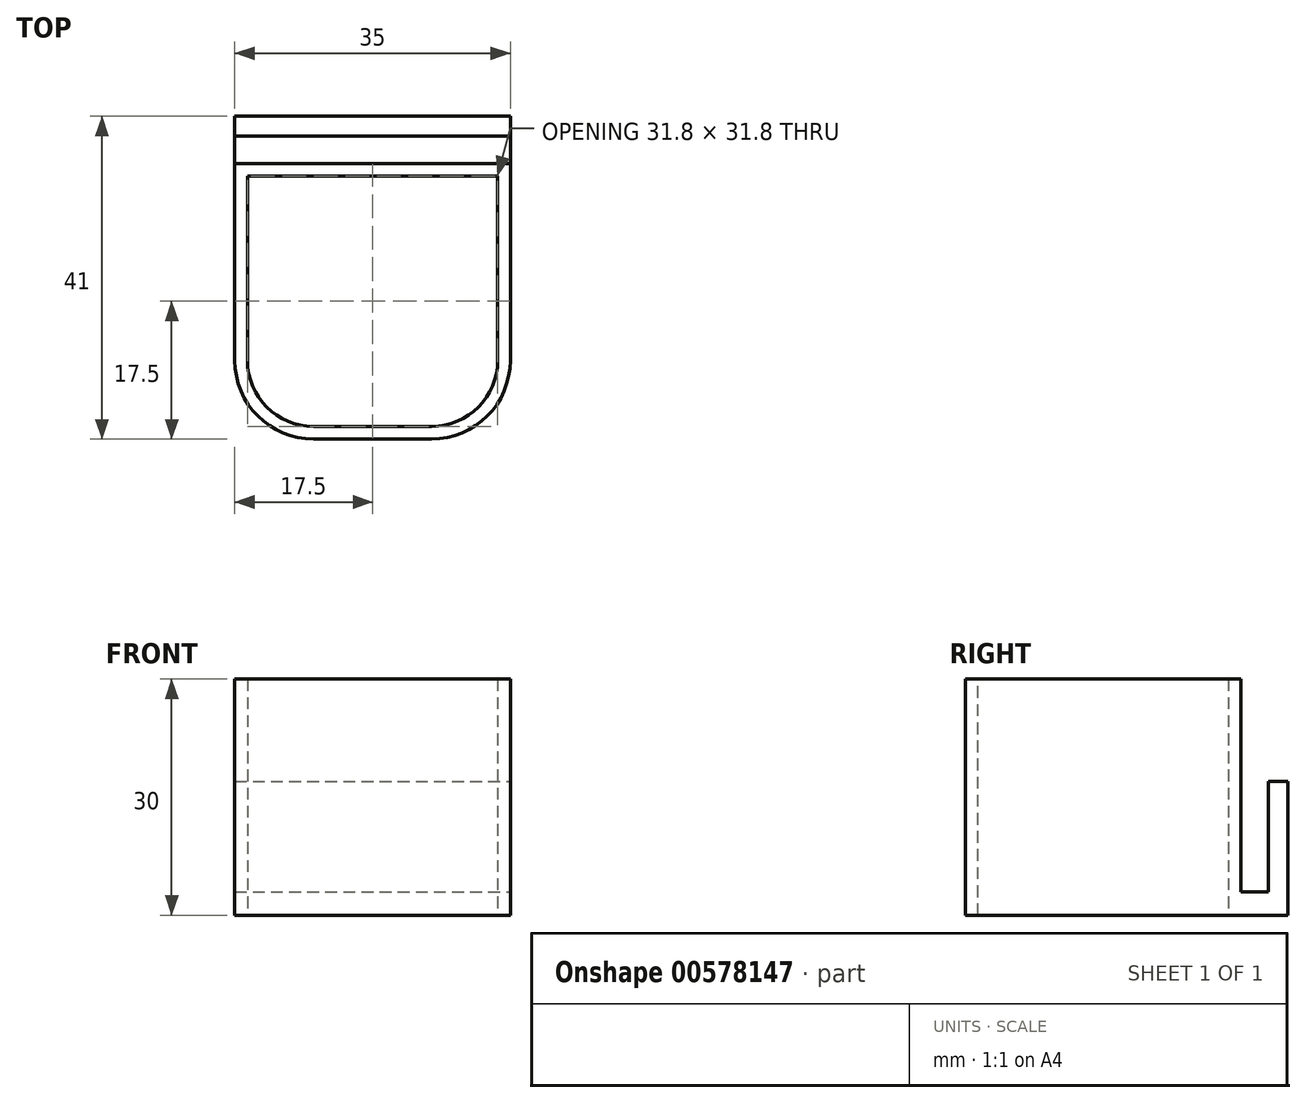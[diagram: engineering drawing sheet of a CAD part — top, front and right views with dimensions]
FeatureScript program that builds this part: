
annotation { "Feature Type Name" : "Feature", "Feature Type Description" : "" }
export const myFeature = defineFeature(function(context is Context, id is Id, definition is map)
    precondition{}
    {
        {
            var Q0;
            Q0=qCreatedBy(makeId("Top.planeOp"),FACE);
            var sketch = newSketch(context, id + "F0", { "sketchPlane" : qUnion([Q0])});
            skLineSegment(sketch, "E0.bottom", {"start": v(0, 0) * mm, "end": v(35, 0) * mm});
            skLineSegment(sketch, "E0.top", {"start": v(0, -2.5) * mm, "end": v(35, -2.5) * mm});
            skLineSegment(sketch, "E0.left", {"start": v(0, 0) * mm, "end": v(0, -2.5) * mm});
            skLineSegment(sketch, "E0.right", {"start": v(35, 0) * mm, "end": v(35, -2.5) * mm});
            skLineSegment(sketch, "E1.top", {"start": v(0, -6) * mm, "end": v(35, -6) * mm});
            skLineSegment(sketch, "E1.left", {"start": v(0, -2.5) * mm, "end": v(0, -6) * mm});
            skLineSegment(sketch, "E1.right", {"start": v(35, -2.5) * mm, "end": v(35, -6) * mm});
            skLineSegment(sketch, "E2.top", {"start": v(10, -41) * mm, "end": v(25, -41) * mm});
            skLineSegment(sketch, "E2.left", {"start": v(0, -6) * mm, "end": v(0, -31) * mm});
            skLineSegment(sketch, "E2.right", {"start": v(35, -6) * mm, "end": v(35, -31) * mm});
            skPoint(sketch, "E3.visualSharp", {"position": v(0, -41) * mm});
            skArc(sketch, "E3.filletArc", {"start": v(0, -31) * mm, "mid": v(2.93, -38.07) * mm, "end": v(10, -41) * mm});
            skPoint(sketch, "E4.visualSharp", {"position": v(35, -41) * mm});
            skArc(sketch, "E4.filletArc", {"start": v(25, -41) * mm, "mid": v(32.07, -38.07) * mm, "end": v(35, -31) * mm});
            skSolve(sketch);
        }
        {
            var Q0;
            Q0=makeQuery(id+"F0.imprint","IMPRINT",FACE,{"disambiguationData":[TD([[makeQuery(id+"F0.imprint","IMPRINT",EDGE,{"derivedFrom":sQuery(id+"F0.wireOp",EDGE,"E1.top")}),-1.0]])]});
            extrude(context, id + "F1", {"entities" : qUnion([Q0]), "depth" : 30 * mm, "offsetDistance" : 25 * mm});
        }
        {
            var Q0;
            Q0=makeQuery(id+"F1.opExtrude","CAP_FACE",FACE,{"disambiguationData":[OSD([sQuery(id+"F0.wireOp",EDGE,"E1.top"),sQuery(id+"F0.wireOp",EDGE,"E2.top"),sQuery(id+"F0.wireOp",EDGE,"E2.left"),sQuery(id+"F0.wireOp",EDGE,"E2.right"),sQuery(id+"F0.wireOp",EDGE,"E3.filletArc"),sQuery(id+"F0.wireOp",EDGE,"E4.filletArc")])],"isStart":false});
            shell(context, id + "F2", {"entities" : qUnion([Q0]), "thickness" : 1.6 * mm});
        }
        {
            var Q0;
            Q0=makeQuery(id+"F0.imprint","IMPRINT",FACE,{"disambiguationData":[TD([[makeQuery(id+"F0.imprint","IMPRINT",EDGE,{"derivedFrom":sQuery(id+"F0.wireOp",EDGE,"E0.top")}),-1.0]])]});
            extrude(context, id + "F3", {"entities" : qUnion([Q0]), "operationType" : NewBodyOperationType.ADD, "depth" : 3 * mm, "offsetDistance" : 25 * mm});
        }
        {
            var Q0;
            Q0=makeQuery(id+"F0.imprint","IMPRINT",FACE,{"disambiguationData":[TD([[makeQuery(id+"F0.imprint","IMPRINT",EDGE,{"derivedFrom":sQuery(id+"F0.wireOp",EDGE,"E0.bottom")}),-1.0]])]});
            extrude(context, id + "F4", {"entities" : qUnion([Q0]), "operationType" : NewBodyOperationType.ADD, "depth" : 17 * mm, "offsetDistance" : 25 * mm});
        }
        {
            var Q0;
            Q0=makeQuery(id+"F2.opShell","OFFSET_FACE",FACE,{"disambiguationData":[OSD([sQuery(id+"F0.wireOp",EDGE,"E1.top"),sQuery(id+"F0.wireOp",EDGE,"E2.top"),sQuery(id+"F0.wireOp",EDGE,"E2.left"),sQuery(id+"F0.wireOp",EDGE,"E2.right"),sQuery(id+"F0.wireOp",EDGE,"E3.filletArc"),sQuery(id+"F0.wireOp",EDGE,"E4.filletArc")])]});
            extrude(context, id + "F5", {"entities" : qUnion([Q0]), "operationType" : NewBodyOperationType.REMOVE, "oppositeDirection" : true, "depth" : 5 * mm, "offsetDistance" : 25 * mm});
        }
    });
